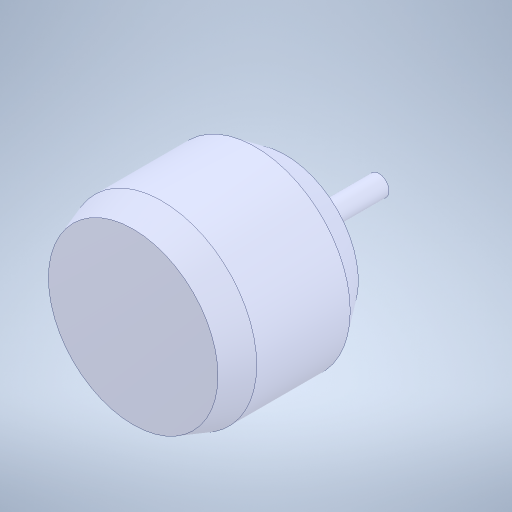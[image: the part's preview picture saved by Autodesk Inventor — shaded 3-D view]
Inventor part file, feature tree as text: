
AUTODESK INVENTOR PART (.ipt)
format: ipt  version: 2023.2 (Build 272271000, 271)  size: 243,200 bytes
history: mixed  units: in
note: dims shown in document units (in); Inventor stores cm internally (conversion verified against a paired STEP export)
features: loft x1, imported_body x1
ambient origin geometry x8: Origin, YZ Plane, XZ Plane, XY Plane, X Axis, Y Axis, Z Axis, Center Point
bodies: Solid1 (imported_parasolid)
feature tree (2):
  loft  "Loft2"
  imported_body  NMx_Import_Brep_tag  [imported B-rep: ~9 faces, bbox_mm=[24.68245, 0.0, 36.2204]]
